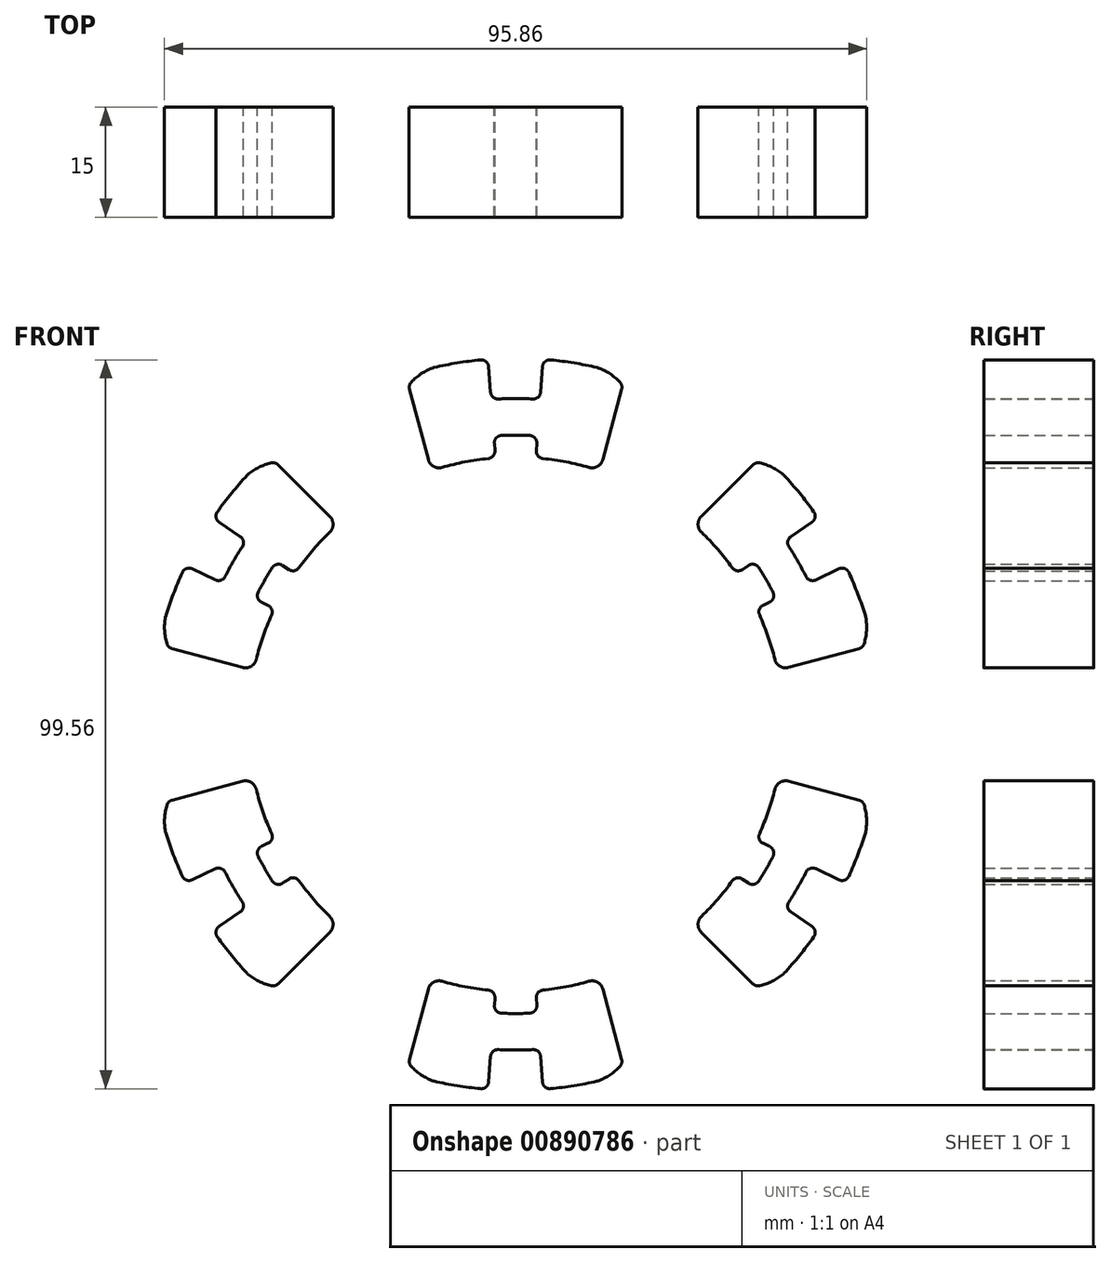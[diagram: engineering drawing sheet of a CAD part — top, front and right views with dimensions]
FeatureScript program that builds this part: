
annotation { "Feature Type Name" : "Feature", "Feature Type Description" : "" }
export const myFeature = defineFeature(function(context is Context, id is Id, definition is map)
    precondition{}
    {
        {
            var Q0;
            Q0=qCreatedBy(makeId("Front.planeOp"),FACE);
            var sketch = newSketch(context, id + "F0", { "sketchPlane" : qUnion([Q0])});
            skLineSegment(sketch, "E0", {"start": v(-14.62, 46.29) * mm, "end": v(-11.9, 36.15) * mm});
            skLineSegment(sketch, "E1", {"start": v(-3.68, 48.85) * mm, "end": v(-3.42, 45.36) * mm});
            skArc(sketch, "E2", {"start": v(0, 44.5) * mm, "mid": v(-1.18, 44.48) * mm, "end": v(-2.37, 44.44) * mm});
            skArc(sketch, "E3", {"start": v(0, 39.5) * mm, "mid": v(-0.97, 39.49) * mm, "end": v(-1.95, 39.45) * mm});
            skLineSegment(sketch, "E4.trimOffspring", {"start": v(-2.9, 38.38) * mm, "end": v(-2.82, 37.38) * mm});
            skArc(sketch, "E5.trimOffspring", {"start": v(-4.77, 49.77) * mm, "mid": v(-9.21, 49.14) * mm, "end": v(-13.58, 48.12) * mm});
            skArc(sketch, "E6.trimOffspring", {"start": v(-3.72, 36.31) * mm, "mid": v(-6.9, 35.84) * mm, "end": v(-10.04, 35.1) * mm});
            skPoint(sketch, "E7.visualSharp", {"position": v(-15, 47.7) * mm});
            skArc(sketch, "E7.filletArc", {"start": v(-13.58, 48.12) * mm, "mid": v(-14.48, 47.42) * mm, "end": v(-14.62, 46.29) * mm});
            skPoint(sketch, "E8.visualSharp", {"position": v(15, 47.7) * mm});
            skPoint(sketch, "E9.visualSharp", {"position": v(11.5, 34.64) * mm});
            skPoint(sketch, "E10.visualSharp", {"position": v(-11.5, 34.64) * mm});
            skArc(sketch, "E10.filletArc", {"start": v(-11.9, 36.15) * mm, "mid": v(-11.2, 35.23) * mm, "end": v(-10.04, 35.1) * mm});
            skPoint(sketch, "E11.visualSharp", {"position": v(-3.75, 49.86) * mm});
            skArc(sketch, "E11.filletArc", {"start": v(-3.68, 48.85) * mm, "mid": v(-4.03, 49.54) * mm, "end": v(-4.77, 49.77) * mm});
            skPoint(sketch, "E12.visualSharp", {"position": v(3.75, 49.86) * mm});
            skPoint(sketch, "E13.visualSharp", {"position": v(3.34, 44.37) * mm});
            skPoint(sketch, "E14.visualSharp", {"position": v(-3.34, 44.37) * mm});
            skArc(sketch, "E14.filletArc", {"start": v(-3.42, 45.36) * mm, "mid": v(-3.08, 44.69) * mm, "end": v(-2.37, 44.44) * mm});
            skPoint(sketch, "E15.visualSharp", {"position": v(-2.97, 39.39) * mm});
            skArc(sketch, "E15.filletArc", {"start": v(-1.95, 39.45) * mm, "mid": v(-2.65, 39.12) * mm, "end": v(-2.9, 38.38) * mm});
            skPoint(sketch, "E16.visualSharp", {"position": v(2.97, 39.39) * mm});
            skPoint(sketch, "E17.visualSharp", {"position": v(2.75, 36.4) * mm});
            skPoint(sketch, "E18.visualSharp", {"position": v(-2.75, 36.4) * mm});
            skArc(sketch, "E18.filletArc", {"start": v(-3.72, 36.31) * mm, "mid": v(-3.05, 36.66) * mm, "end": v(-2.82, 37.38) * mm});
            skLineSegment(sketch, "E19", {"start": v(0, 44.5) * mm, "end": v(0, 39.5) * mm});
            skSolve(sketch);
        }
        {
            var Q0;
            Q0 = qSketchRegion(id + "F0", true);
            extrude(context, id + "F1", {"entities" : qUnion([Q0]), "depth" : 15 * mm, "offsetDistance" : 25 * mm});
        }
        {
            var Q0;
            Q0=makeQuery(id+"F1.opExtrude","CAP_FACE",FACE,{"disambiguationData":[OSD([sQuery(id+"F0.wireOp",EDGE,"9F88evCj-wvHZ-jU9Q-vnWg-NcqEs7H0BCUU"),sQuery(id+"F0.wireOp",EDGE,"E0"),sQuery(id+"F0.wireOp",EDGE,"E1"),sQuery(id+"F0.wireOp",EDGE,"Jh07TOeY-yO65-X3NJ-Uf7U-KrOvsrUDv6FE"),sQuery(id+"F0.wireOp",EDGE,"E2"),sQuery(id+"F0.wireOp",EDGE,"E3"),sQuery(id+"F0.wireOp",EDGE,"E4.trimOffspring"),sQuery(id+"F0.wireOp",EDGE,"a817e8e5-6a07-4a55-bb10-5e5b8f971b3a.trimOffspring"),sQuery(id+"F0.wireOp",EDGE,"HOBfTaWE-fcK8-fJNQ-9TiI-jfp7etbn9sGY"),sQuery(id+"F0.wireOp",EDGE,"AAxgkpiT-gA59-I4OI-SFvA-ItI4TH1vOWE4"),sQuery(id+"F0.wireOp",EDGE,"E5.trimOffspring"),sQuery(id+"F0.wireOp",EDGE,"E6.trimOffspring"),sQuery(id+"F0.wireOp",EDGE,"E7.filletArc"),sQuery(id+"F0.wireOp",EDGE,"E8.filletArc"),sQuery(id+"F0.wireOp",EDGE,"E9.filletArc"),sQuery(id+"F0.wireOp",EDGE,"E10.filletArc"),sQuery(id+"F0.wireOp",EDGE,"E11.filletArc"),sQuery(id+"F0.wireOp",EDGE,"E12.filletArc"),sQuery(id+"F0.wireOp",EDGE,"E13.filletArc"),sQuery(id+"F0.wireOp",EDGE,"E14.filletArc"),sQuery(id+"F0.wireOp",EDGE,"E15.filletArc"),sQuery(id+"F0.wireOp",EDGE,"E16.filletArc"),sQuery(id+"F0.wireOp",EDGE,"E17.filletArc"),sQuery(id+"F0.wireOp",EDGE,"E18.filletArc")])],"isStart":false});
            var sketch = newSketch(context, id + "F2", { "sketchPlane" : qUnion([Q0])});
            skArc(sketch, "E20", {"start": v(-9.21, 49.14) * mm, "mid": v(-12.22, 48.28) * mm, "end": v(-14.62, 46.29) * mm});
            skLineSegment(sketch, "E21", {"start": v(-9.21, 49.14) * mm, "end": v(-9.48, 50.32) * mm});
            skLineSegment(sketch, "E22", {"start": v(-9.48, 50.32) * mm, "end": v(-17.06, 47.3) * mm});
            skLineSegment(sketch, "E23", {"start": v(-17.06, 47.3) * mm, "end": v(-14.62, 46.29) * mm});
            skSolve(sketch);
        }
        {
            var Q0;
            Q0 = qSketchRegion(id + "F2", true);
            extrude(context, id + "F3", {"entities" : qUnion([Q0]), "operationType" : NewBodyOperationType.REMOVE, "oppositeDirection" : true, "depth" : 25 * mm, "offsetDistance" : 25 * mm});
        }
        {
            var Q0;
            {var subQ0=sQuery(id+"F0.wireOp",EDGE,"E7.filletArc");var subQ1=sQuery(id+"F0.wireOp",EDGE,"E0");Q0=makeQuery(id+"F3.boolean.opBoolean","MERGE",EDGE,{"derivedFrom":[makeQuery(id+"F1.opExtrude","SWEPT_EDGE",EDGE,{"disambiguationData":[OSD([subQ1,subQ0])]})],"fromTools":[makeQuery(id+"F3.opExtrude","SWEPT_EDGE",EDGE,{"disambiguationData":[OSD([subQ1,subQ0,sQuery(id+"F2.wireOp",EDGE,"E20"),sQuery(id+"F2.wireOp",EDGE,"E23")])]})]});}
            var Q1;
            Q1=makeQuery(id+"F3.boolean.opBoolean","INTERSECT",EDGE,{"derivedFrom":[makeQuery(id+"F1.opExtrude","SWEPT_FACE",FACE,{"disambiguationData":[OSD([sQuery(id+"F0.wireOp",EDGE,"E5.trimOffspring")])]}),makeQuery(id+"F3.opExtrude","SWEPT_FACE",FACE,{"disambiguationData":[OSD([sQuery(id+"F2.wireOp",EDGE,"E20")])]})]});
            fillet(context, id + "F4", {"entities" : qUnion([Q0, Q1]), "radius" : 1 * mm, "tangentPropagation" : true, "allowEdgeOverflow" : false});
        }
        {
            var Q0;
            Q0=makeQuery(id+"F1.opExtrude","SWEPT_BODY",BODY,{"disambiguationData":[OSD([sQuery(id+"F0.wireOp",EDGE,"E0"),sQuery(id+"F0.wireOp",EDGE,"E1"),sQuery(id+"F0.wireOp",EDGE,"E2"),sQuery(id+"F0.wireOp",EDGE,"E3"),sQuery(id+"F0.wireOp",EDGE,"E4.trimOffspring"),sQuery(id+"F0.wireOp",EDGE,"E5.trimOffspring"),sQuery(id+"F0.wireOp",EDGE,"E6.trimOffspring"),sQuery(id+"F0.wireOp",EDGE,"E7.filletArc"),sQuery(id+"F0.wireOp",EDGE,"E10.filletArc"),sQuery(id+"F0.wireOp",EDGE,"E11.filletArc"),sQuery(id+"F0.wireOp",EDGE,"E14.filletArc"),sQuery(id+"F0.wireOp",EDGE,"E15.filletArc"),sQuery(id+"F0.wireOp",EDGE,"E18.filletArc"),sQuery(id+"F0.wireOp",EDGE,"E19")])]});
            var Q1;
            Q1=qCreatedBy(makeId("Right.planeOp"),FACE);
            mirror(context, id + "F5", {"operationType" : NewBodyOperationType.ADD, "entities" : qUnion([Q0]), "mirrorPlane" : qUnion([Q1])});
        }
        {
            var Q0;
            Q0=makeQuery(id+"F1.opExtrude","SWEPT_BODY",BODY,{"disambiguationData":[OSD([sQuery(id+"F0.wireOp",EDGE,"E0"),sQuery(id+"F0.wireOp",EDGE,"E1"),sQuery(id+"F0.wireOp",EDGE,"E2"),sQuery(id+"F0.wireOp",EDGE,"E3"),sQuery(id+"F0.wireOp",EDGE,"E4.trimOffspring"),sQuery(id+"F0.wireOp",EDGE,"E5.trimOffspring"),sQuery(id+"F0.wireOp",EDGE,"E6.trimOffspring"),sQuery(id+"F0.wireOp",EDGE,"E7.filletArc"),sQuery(id+"F0.wireOp",EDGE,"E10.filletArc"),sQuery(id+"F0.wireOp",EDGE,"E11.filletArc"),sQuery(id+"F0.wireOp",EDGE,"E14.filletArc"),sQuery(id+"F0.wireOp",EDGE,"E15.filletArc"),sQuery(id+"F0.wireOp",EDGE,"E18.filletArc"),sQuery(id+"F0.wireOp",EDGE,"E19")])]});
            var Q1;
            Q1=makeQuery(id+"F1.opExtrude","SWEPT_FACE",FACE,{"disambiguationData":[OSD([sQuery(id+"F0.wireOp",EDGE,"E6.trimOffspring")])]});
            circularPattern(context, id + "F6", {"entities" : qUnion([Q0]), "axis" : qUnion([Q1]), "angle" : 360 * degree, "instanceCount" : 6, "equalSpace" : true});
        }
    });
